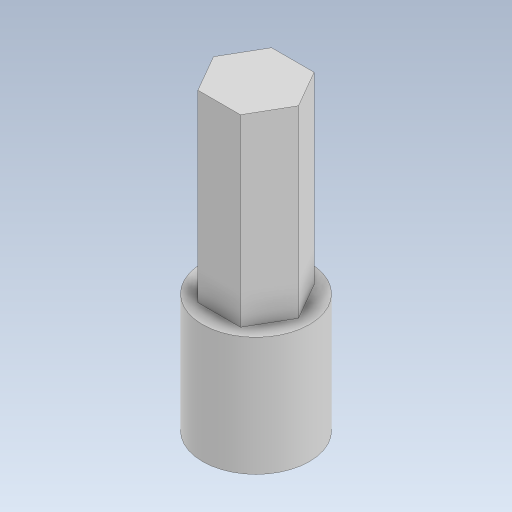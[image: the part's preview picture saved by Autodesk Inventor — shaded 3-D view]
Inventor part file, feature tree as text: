
AUTODESK INVENTOR PART (.ipt)
format: ipt  version: 2023.5 (Build 275446000, 446)  size: 329,216 bytes
history: native  units: mm
features: extrude x7, sketch x5, hole x1
ambient origin geometry x8: Origin, YZ Plane, XZ Plane, XY Plane, X Axis, Y Axis, Z Axis, Center Point
bodies: Solid1 (feature_tree), Solid2 (feature_tree)
feature tree (13):
  extrude  "Extrusion2"  Depth=2.38mm TaperAngle=0.0deg
  extrude  "Extrusion3"  Depth=7.0mm
  extrude  "Extrusion4"  Depth=9.0mm
  extrude  "Extrusion5"  Depth=10.0mm
  extrude  "Extrusion10"  Depth=10.0mm TaperAngle=0.0deg
  extrude  "Extrusion6"  Depth=10.0mm TaperAngle=0.0deg
  hole  "Hole1"  [1 undecoded]
  extrude  "Extrusion1"  Depth=10.0mm TaperAngle=0.0deg
  sketch  "Sketch6"  dims[d0=25.0mm d1=2.38mm d2=0.0mm]
  sketch  "Sketch7"  dims[d3=4.0mm d4=7.0mm]
  sketch  "Sketch9"  dims[d5=3.5mm d6=9.0mm]
  sketch  "Sketch10"  dims[d7=10.0mm d8=0.0mm d9=4.0mm]
  sketch  "Sketch14"  dims[d10=3.5mm d11=10.0mm d12=0.0mm d13=2.0mm d14=0.0mm d15=7.16mm d16=15.5mm d17=0.0mm d18=0.75mm d19=0.0mm d21=2.0mm d22=2.25mm d23=0.0mm d24=2.0mm d25=6.0mm d26=4.0mm d27=2.0mm d28=90.0deg d29=3.33mm d30=0.0mm d38=2.0mm d39=4.0mm d40=0.0mm d34=0.5mm d35=0.872665mm d36=0.5mm d37=0.872665mm d41=0.872665mm]
note: 1 required parameter value undecoded (feature->parameter linkage not recoverable at this tier; creation-order binding heuristic only, values carry confidence <= 0.55)
